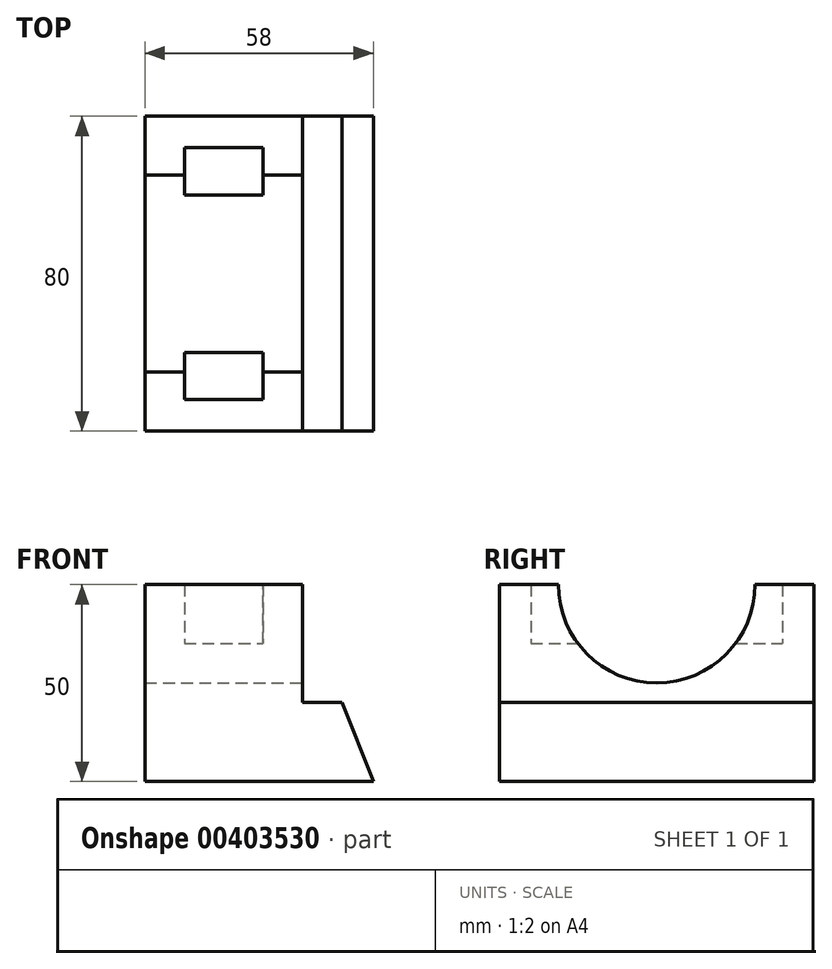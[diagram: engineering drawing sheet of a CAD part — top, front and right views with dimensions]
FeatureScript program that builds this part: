
annotation { "Feature Type Name" : "Feature", "Feature Type Description" : "" }
export const myFeature = defineFeature(function(context is Context, id is Id, definition is map)
    precondition{}
    {
        {
            var Q0;
            Q0=qCreatedBy(makeId("Right.planeOp"),FACE);
            var sketch = newSketch(context, id + "F0", { "sketchPlane" : qUnion([Q0])});
            skLineSegment(sketch, "E0", {"start": v(-40.45, 21.24) * mm, "end": v(-40.45, -8.76) * mm});
            skLineSegment(sketch, "E1", {"start": v(-40.45, -8.76) * mm, "end": v(39.55, -8.76) * mm});
            skLineSegment(sketch, "E2", {"start": v(39.55, -8.76) * mm, "end": v(39.55, 21.24) * mm});
            skLineSegment(sketch, "E3", {"start": v(-0.45, -8.76) * mm, "end": v(-0.45, 21.24) * mm, "construction": true});
            skLineSegment(sketch, "E4", {"start": v(-40.45, 21.24) * mm, "end": v(-25.45, 21.24) * mm});
            skArc(sketch, "E5", {"start": v(-25.45, 21.24) * mm, "mid": v(-0.45, -3.76) * mm, "end": v(24.55, 21.24) * mm});
            skLineSegment(sketch, "E6", {"start": v(39.55, 21.24) * mm, "end": v(24.55, 21.24) * mm});
            skSolve(sketch);
        }
        {
            var Q0;
            Q0 = qSketchRegion(id + "F0", true);
            extrude(context, id + "F1", {"entities" : qUnion([Q0]), "oppositeDirection" : true, "depth" : 40 * mm});
        }
        {
            var Q0;
            Q0=makeQuery(id+"F1.opExtrude","SWEPT_FACE",FACE,{"disambiguationData":[OSD([sQuery(id+"F0.wireOp",EDGE,"E0")])]});
            var sketch = newSketch(context, id + "F2", { "sketchPlane" : qUnion([Q0])});
            skLineSegment(sketch, "E7", {"start": v(-40, -8.76) * mm, "end": v(10, -8.76) * mm});
            skLineSegment(sketch, "E8", {"start": v(10, -8.76) * mm, "end": v(18, -28.76) * mm});
            skLineSegment(sketch, "E9", {"start": v(18, -28.76) * mm, "end": v(-40, -28.76) * mm});
            skLineSegment(sketch, "E10", {"start": v(-40, -28.76) * mm, "end": v(-40, -8.76) * mm});
            skSolve(sketch);
        }
        {
            var Q0;
            Q0 = qSketchRegion(id + "F2", true);
            var Q1;
            Q1=makeQuery(id+"F1.opExtrude","SWEPT_FACE",FACE,{"disambiguationData":[OSD([sQuery(id+"F0.wireOp",EDGE,"E2")])]});
            extrude(context, id + "F3", {"entities" : qUnion([Q0]), "operationType" : NewBodyOperationType.ADD, "endBound" : BoundingType.UP_TO_SURFACE, "oppositeDirection" : true, "endBoundEntityFace" : qUnion([Q1]), "depth" : 25 * mm});
        }
        {
            var Q0;
            {var subQ0=sQuery(id+"F0.wireOp",EDGE,"E2");Q0=makeQuery(id+"F3.boolean.opBoolean","MERGE",FACE,{"derivedFrom":[makeQuery(id+"F1.opExtrude","SWEPT_FACE",FACE,{"disambiguationData":[OSD([subQ0])]}),makeQuery(id+"F3.opExtrude","CAP_FACE",FACE,{"disambiguationData":[OSD([subQ0])],"isStart":false})]});}
            cPlane(context, id + "F4", {"entities" : qUnion([Q0]), "cplaneType" : CPlaneType.OFFSET, "offset" : ((80 - 64) / 2) * mm, "oppositeDirection" : true, "width" : 150 * mm, "height" : 150 * mm});
        }
        {
            var Q0;
            Q0=qCreatedBy(id+"F4.planeOp",FACE);
            var sketch = newSketch(context, id + "F5", { "sketchPlane" : qUnion([Q0])});
            skLineSegment(sketch, "E11.bottom", {"start": v(10, 21.24) * mm, "end": v(30, 21.24) * mm});
            skLineSegment(sketch, "E11.top", {"start": v(10, 6.24) * mm, "end": v(30, 6.24) * mm});
            skLineSegment(sketch, "E11.left", {"start": v(10, 21.24) * mm, "end": v(10, 6.24) * mm});
            skLineSegment(sketch, "E11.right", {"start": v(30, 21.24) * mm, "end": v(30, 6.24) * mm});
            skSolve(sketch);
        }
        {
            var Q0;
            Q0 = qSketchRegion(id + "F5", true);
            extrude(context, id + "F6", {"entities" : qUnion([Q0]), "operationType" : NewBodyOperationType.REMOVE, "oppositeDirection" : true, "depth" : 64 * mm});
        }
    });
